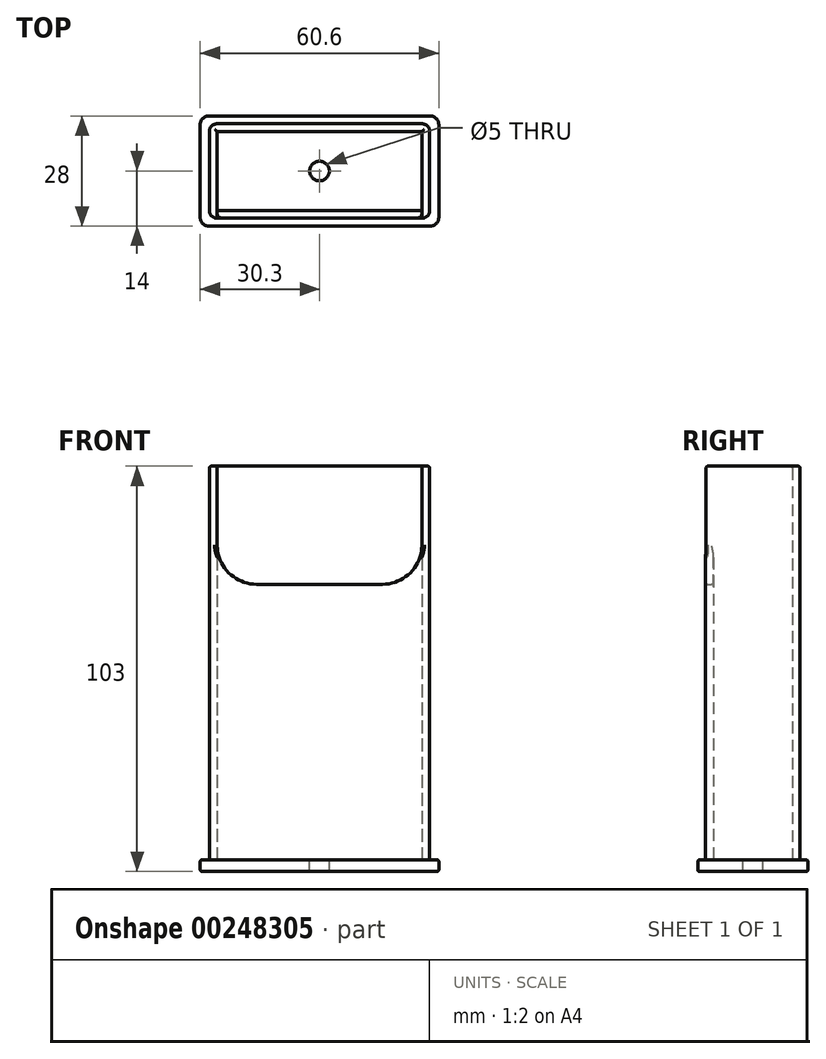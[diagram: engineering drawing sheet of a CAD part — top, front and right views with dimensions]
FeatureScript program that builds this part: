
annotation { "Feature Type Name" : "Feature", "Feature Type Description" : "" }
export const myFeature = defineFeature(function(context is Context, id is Id, definition is map)
    precondition{}
    {
        {
            var Q0;
            Q0=qCreatedBy(makeId("Top.planeOp"),FACE);
            var sketch = newSketch(context, id + "F0", { "sketchPlane" : qUnion([Q0])});
            skLineSegment(sketch, "E0.bottom", {"start": v(-26, -10) * mm, "end": v(26, -10) * mm});
            skLineSegment(sketch, "E0.top", {"start": v(-26, 10) * mm, "end": v(26, 10) * mm});
            skLineSegment(sketch, "E0.left", {"start": v(-26, -10) * mm, "end": v(-26, 10) * mm});
            skLineSegment(sketch, "E0.right", {"start": v(26, -10) * mm, "end": v(26, 10) * mm});
            skPoint(sketch, "E0.middle", {"position": v(0, 0) * mm});
            skLineSegment(sketch, "E1.bottom", {"start": v(-26, 12) * mm, "end": v(26, 12) * mm});
            skLineSegment(sketch, "E1.top", {"start": v(-26, -12) * mm, "end": v(26, -12) * mm});
            skLineSegment(sketch, "E1.left", {"start": v(-28, 10) * mm, "end": v(-28, -10) * mm});
            skLineSegment(sketch, "E1.right", {"start": v(28, 10) * mm, "end": v(28, -10) * mm});
            skPoint(sketch, "E2.visualSharp", {"position": v(-28, 12) * mm});
            skArc(sketch, "E2.filletArc", {"start": v(-26, 12) * mm, "mid": v(-27.41, 11.41) * mm, "end": v(-28, 10) * mm});
            skPoint(sketch, "E3.visualSharp", {"position": v(28, 12) * mm});
            skArc(sketch, "E3.filletArc", {"start": v(28, 10) * mm, "mid": v(27.41, 11.41) * mm, "end": v(26, 12) * mm});
            skPoint(sketch, "E4.visualSharp", {"position": v(28, -12) * mm});
            skArc(sketch, "E4.filletArc", {"start": v(26, -12) * mm, "mid": v(27.41, -11.41) * mm, "end": v(28, -10) * mm});
            skPoint(sketch, "E5.visualSharp", {"position": v(-28, -12) * mm});
            skArc(sketch, "E5.filletArc", {"start": v(-28, -10) * mm, "mid": v(-27.41, -11.41) * mm, "end": v(-26, -12) * mm});
            skSolve(sketch);
        }
        {
            var Q0;
            Q0 = qSketchRegion(id + "F0", true);
            extrude(context, id + "F1", {"entities" : qUnion([Q0]), "depth" : 100 * mm});
        }
        {
            var Q0;
            Q0=qCreatedBy(makeId("Top.planeOp"),FACE);
            var sketch = newSketch(context, id + "F2", { "sketchPlane" : qUnion([Q0])});
            skLineSegment(sketch, "E6.bottom", {"start": v(28.1, 14) * mm, "end": v(-28.1, 14) * mm});
            skLineSegment(sketch, "E6.top", {"start": v(28.1, -14) * mm, "end": v(-28.1, -14) * mm});
            skLineSegment(sketch, "E6.left", {"start": v(30.3, 11.8) * mm, "end": v(30.3, -11.8) * mm});
            skLineSegment(sketch, "E6.right", {"start": v(-30.3, 11.8) * mm, "end": v(-30.3, -11.8) * mm});
            skPoint(sketch, "E6.middle", {"position": v(0, 0) * mm});
            skPoint(sketch, "E7.visualSharp", {"position": v(-30.3, -14) * mm});
            skArc(sketch, "E7.filletArc", {"start": v(-30.3, -11.8) * mm, "mid": v(-29.66, -13.36) * mm, "end": v(-28.1, -14) * mm});
            skPoint(sketch, "E8.visualSharp", {"position": v(-30.3, 14) * mm});
            skArc(sketch, "E8.filletArc", {"start": v(-28.1, 14) * mm, "mid": v(-29.66, 13.36) * mm, "end": v(-30.3, 11.8) * mm});
            skPoint(sketch, "E9.visualSharp", {"position": v(30.3, 14) * mm});
            skArc(sketch, "E9.filletArc", {"start": v(30.3, 11.8) * mm, "mid": v(29.66, 13.36) * mm, "end": v(28.1, 14) * mm});
            skPoint(sketch, "E10.visualSharp", {"position": v(30.3, -14) * mm});
            skArc(sketch, "E10.filletArc", {"start": v(28.1, -14) * mm, "mid": v(29.66, -13.36) * mm, "end": v(30.3, -11.8) * mm});
            skCircle(sketch, "E11", {"center": v(0, 0) * mm, "radius": 2.5 * mm});
            skSolve(sketch);
        }
        {
            var Q0;
            Q0 = qSketchRegion(id + "F2", true);
            extrude(context, id + "F3", {"entities" : qUnion([Q0]), "operationType" : NewBodyOperationType.ADD, "oppositeDirection" : true, "depth" : 3 * mm});
        }
        {
            var Q0;
            Q0=qCreatedBy(makeId("Front.planeOp"),FACE);
            var sketch = newSketch(context, id + "F4", { "sketchPlane" : qUnion([Q0])});
            skLineSegment(sketch, "E12.bottom", {"start": v(-26, 100) * mm, "end": v(26, 100) * mm});
            skLineSegment(sketch, "E12.top", {"start": v(-16, 70) * mm, "end": v(16, 70) * mm});
            skLineSegment(sketch, "E12.left", {"start": v(-26, 100) * mm, "end": v(-26, 80) * mm});
            skLineSegment(sketch, "E12.right", {"start": v(26, 100) * mm, "end": v(26, 80) * mm});
            skPoint(sketch, "E12.middle", {"position": v(0, 85) * mm});
            skPoint(sketch, "E13.visualSharp", {"position": v(-26, 70) * mm});
            skArc(sketch, "E13.filletArc", {"start": v(-26, 80) * mm, "mid": v(-23.07, 72.93) * mm, "end": v(-16, 70) * mm});
            skPoint(sketch, "E14.visualSharp", {"position": v(26, 70) * mm});
            skArc(sketch, "E14.filletArc", {"start": v(16, 70) * mm, "mid": v(23.07, 72.93) * mm, "end": v(26, 80) * mm});
            skSolve(sketch);
        }
        {
            var Q0;
            Q0 = qSketchRegion(id + "F4", true);
            extrude(context, id + "F5", {"entities" : qUnion([Q0]), "operationType" : NewBodyOperationType.REMOVE, "endBound" : BoundingType.THROUGH_ALL, "depth" : 25 * mm});
        }
        {
            var Q0;
            Q0=makeQuery(id+"F3.opExtrude","CAP_FACE",FACE,{"disambiguationData":[OSD([sQuery(id+"F2.wireOp",EDGE,"E6.bottom"),sQuery(id+"F2.wireOp",EDGE,"E6.top"),sQuery(id+"F2.wireOp",EDGE,"E6.left"),sQuery(id+"F2.wireOp",EDGE,"E6.right"),sQuery(id+"F2.wireOp",EDGE,"E7.filletArc"),sQuery(id+"F2.wireOp",EDGE,"E8.filletArc"),sQuery(id+"F2.wireOp",EDGE,"E9.filletArc"),sQuery(id+"F2.wireOp",EDGE,"E10.filletArc"),sQuery(id+"F2.wireOp",EDGE,"E11")])],"isStart":false});
            var Q1;
            Q1=makeQuery(id+"F3.opExtrude","CAP_EDGE",EDGE,{"disambiguationData":[OSD([sQuery(id+"F2.wireOp",EDGE,"E7.filletArc")])],"isStart":true});
            var Q2;
            Q2=makeQuery(id+"F1.opExtrude","CAP_FACE",FACE,{"disambiguationData":[OSD([sQuery(id+"F0.wireOp",EDGE,"E0.bottom"),sQuery(id+"F0.wireOp",EDGE,"E0.top"),sQuery(id+"F0.wireOp",EDGE,"E0.left"),sQuery(id+"F0.wireOp",EDGE,"E0.right"),sQuery(id+"F0.wireOp",EDGE,"E1.bottom"),sQuery(id+"F0.wireOp",EDGE,"E1.top"),sQuery(id+"F0.wireOp",EDGE,"E1.left"),sQuery(id+"F0.wireOp",EDGE,"E1.right"),sQuery(id+"F0.wireOp",EDGE,"E2.filletArc"),sQuery(id+"F0.wireOp",EDGE,"E3.filletArc"),sQuery(id+"F0.wireOp",EDGE,"E4.filletArc"),sQuery(id+"F0.wireOp",EDGE,"E5.filletArc")])],"isStart":false});
            var Q3;
            Q3=makeQuery(id+"F5.boolean.opBoolean","COPY",FACE,{"derivedFrom":makeQuery(id+"F5.opExtrude","SWEPT_FACE",FACE,{"disambiguationData":[OSD([sQuery(id+"F4.wireOp",EDGE,"E12.top")])]})});
            fillet(context, id + "F6", {"entities" : qUnion([Q0, Q1, Q2, Q3]), "radius" : .5 * mm, "tangentPropagation" : true, "allowEdgeOverflow" : false});
        }
    });
